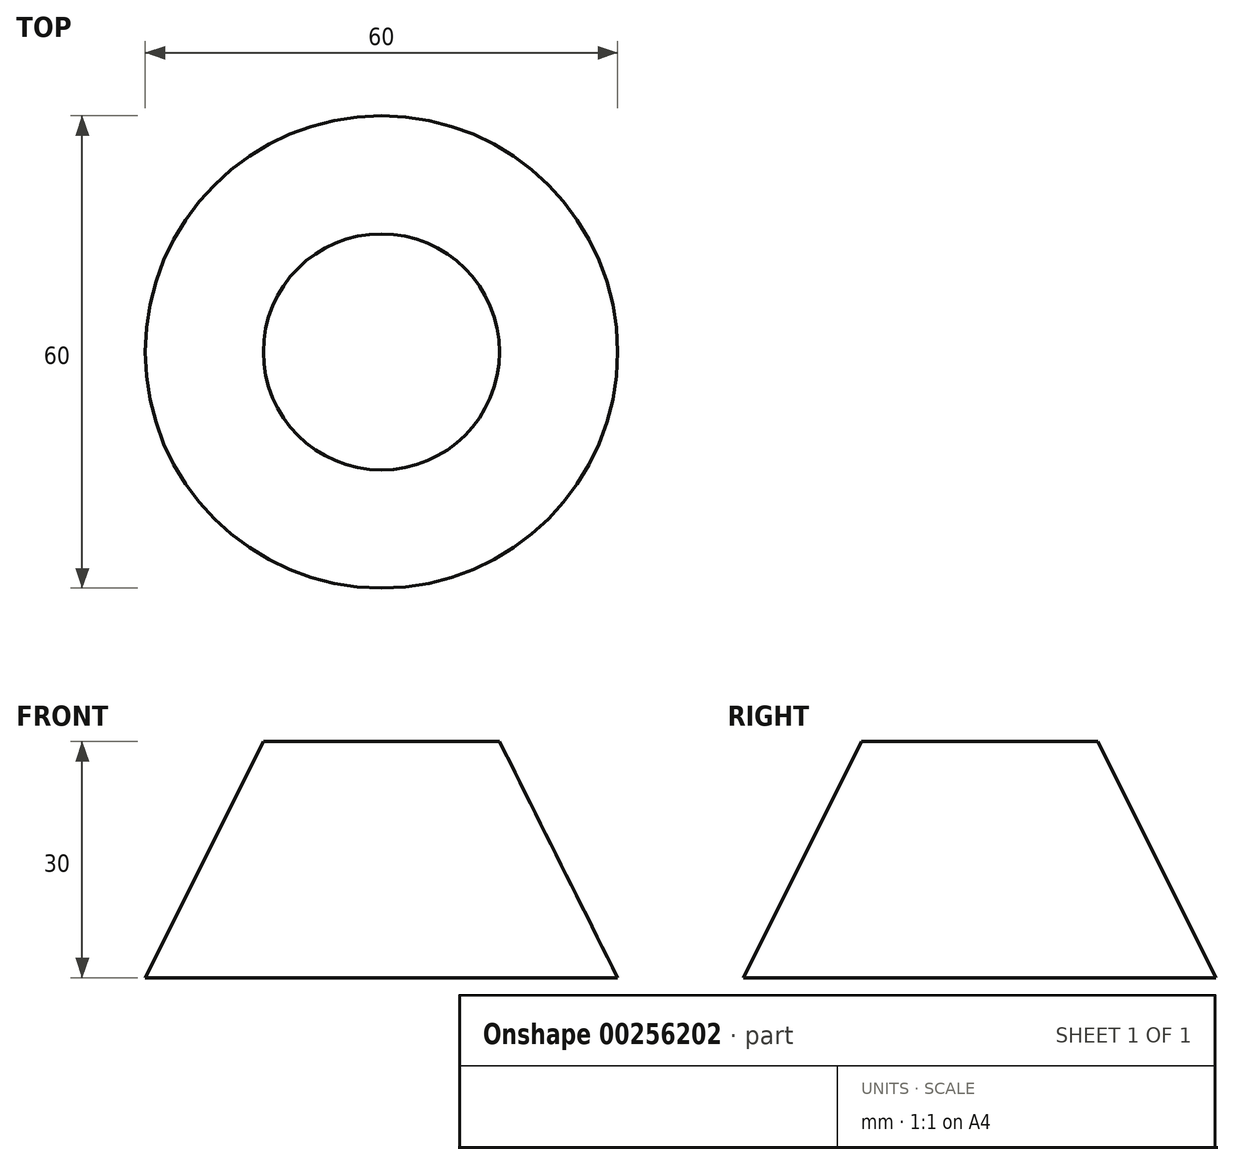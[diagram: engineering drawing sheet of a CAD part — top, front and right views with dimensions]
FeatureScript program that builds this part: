
annotation { "Feature Type Name" : "Feature", "Feature Type Description" : "" }
export const myFeature = defineFeature(function(context is Context, id is Id, definition is map)
    precondition{}
    {
        {
            var Q0;
            Q0=qCreatedBy(makeId("Front.planeOp"),FACE);
            var sketch = newSketch(context, id + "F0", { "sketchPlane" : qUnion([Q0])});
            skLineSegment(sketch, "E0", {"start": v(0, 0) * mm, "end": v(0, 30) * mm});
            skLineSegment(sketch, "E1", {"start": v(0, 30) * mm, "end": v(15, 30) * mm});
            skLineSegment(sketch, "E2", {"start": v(15, 30) * mm, "end": v(30, 0) * mm});
            skLineSegment(sketch, "E3", {"start": v(30, 0) * mm, "end": v(0, 0) * mm});
            skLineSegment(sketch, "E4", {"start": v(0, 70.14) * mm, "end": v(0, -49.49) * mm, "construction": true});
            skSolve(sketch);
        }
        {
            var Q0;
            Q0=makeQuery(id+"F0.imprint","IMPRINT",FACE,{"disambiguationData":[TD([[makeQuery(id+"F0.imprint","IMPRINT",EDGE,{"derivedFrom":sQuery(id+"F0.wireOp",EDGE,"E0")}),-1.0]])]});
            var Q1;
            Q1=sQuery(id+"F0.wireOp",EDGE,"E1");
            var Q2;
            Q2=sQuery(id+"F0.wireOp",EDGE,"E2");
            var Q3;
            Q3=sQuery(id+"F0.wireOp",EDGE,"E3");
            var Q4;
            Q4=sQuery(id+"F0.wireOp",EDGE,"E0");
            var Q5;
            Q5=sQuery(id+"F0.wireOp",EDGE,"E4");
            revolve(context, id + "F1", {"entities" : qUnion([Q0]), "surfaceEntities" : qUnion([Q1, Q2, Q3, Q4]), "axis" : qUnion([Q5]), "revolveType" : RevolveType.FULL});
        }
    });
